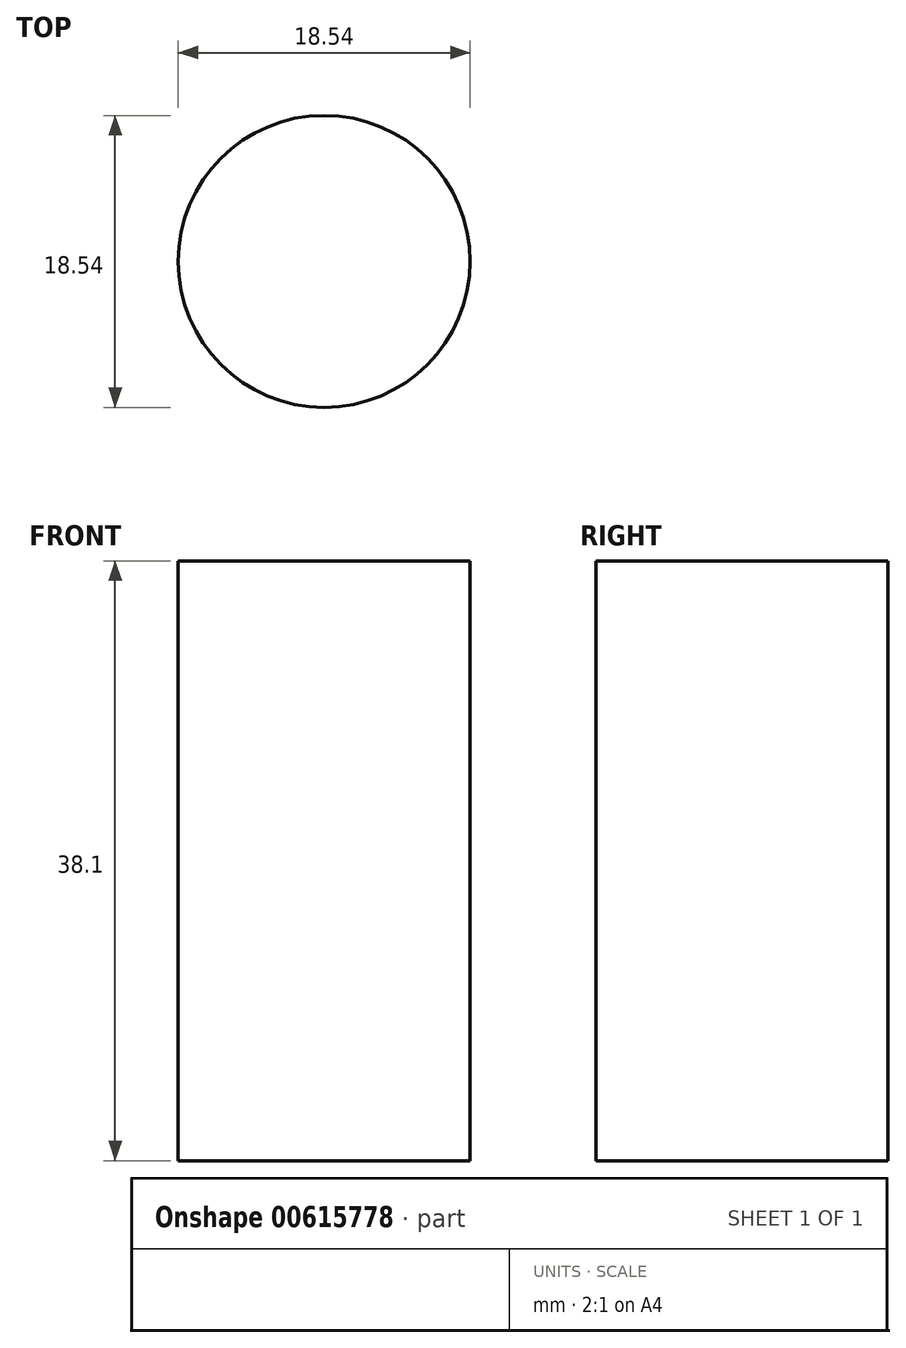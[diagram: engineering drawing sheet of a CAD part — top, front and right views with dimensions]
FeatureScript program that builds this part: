
annotation { "Feature Type Name" : "Feature", "Feature Type Description" : "" }
export const myFeature = defineFeature(function(context is Context, id is Id, definition is map)
    precondition{}
    {
        {
            var Q0;
            Q0=qCreatedBy(makeId("Top.planeOp"),FACE);
            var sketch = newSketch(context, id + "F0", { "sketchPlane" : qUnion([Q0])});
            skCircle(sketch, "E0", {"center": v(0, 0) * mm, "radius": 9.27 * mm});
            skSolve(sketch);
        }
        {
            var Q0;
            Q0=makeQuery(id+"F0.imprint","IMPRINT",FACE,{"disambiguationData":[TD([[makeQuery(id+"F0.imprint","IMPRINT",EDGE,{"derivedFrom":sQuery(id+"F0.wireOp",EDGE,"E0")}),1.0]])]});
            extrude(context, id + "F1", {"entities" : qUnion([Q0]), "depth" : 38.1 * mm, "offsetDistance" : 25.4 * mm});
        }
    });
